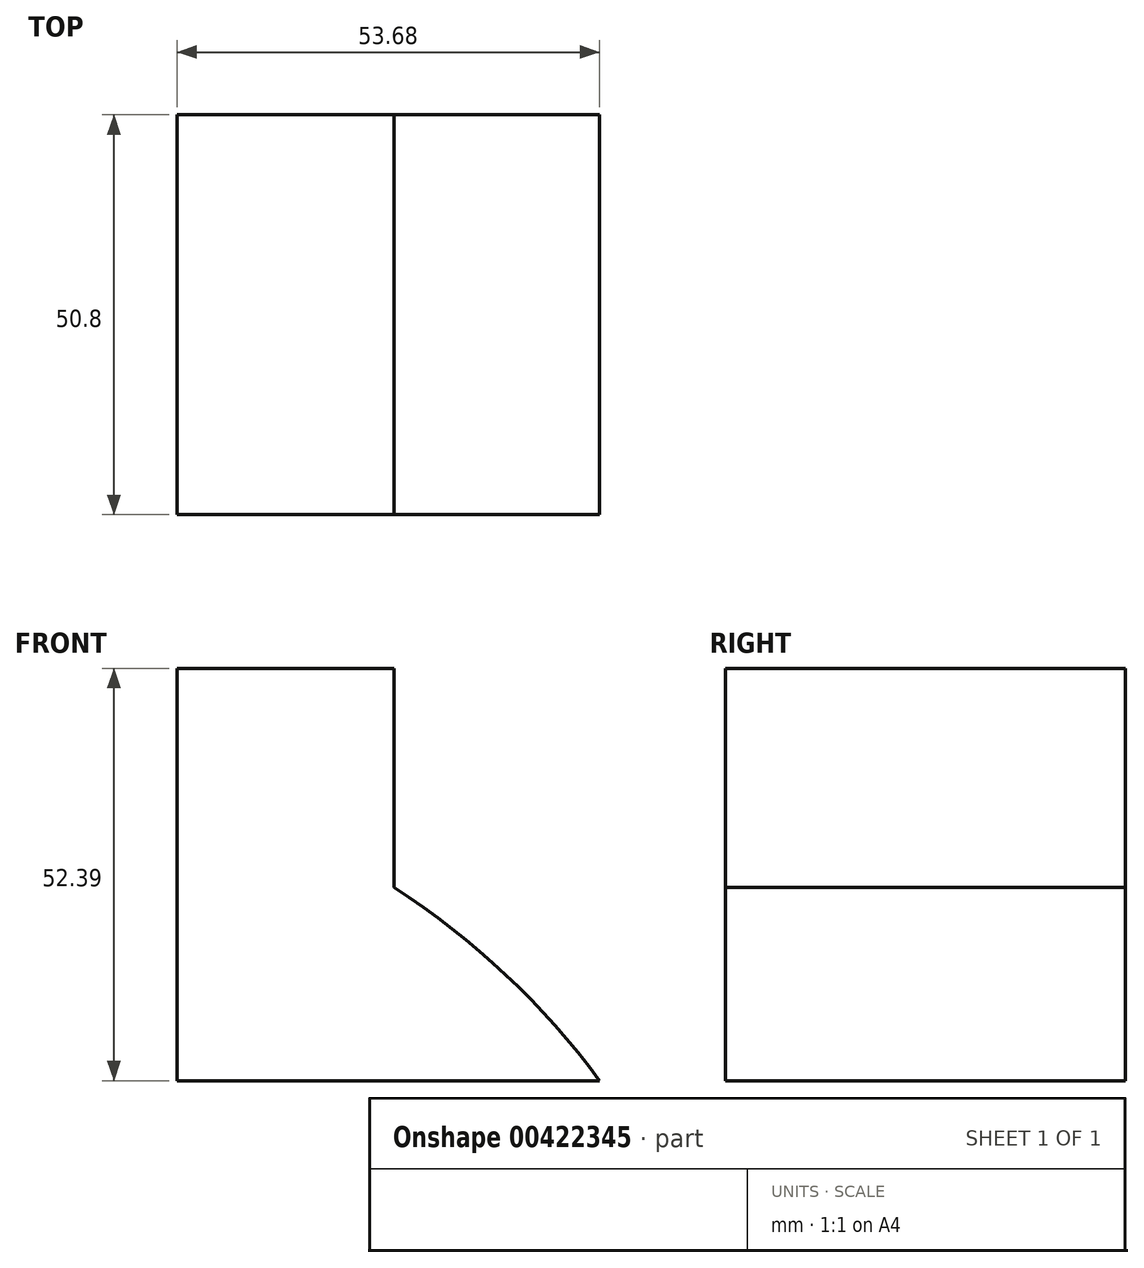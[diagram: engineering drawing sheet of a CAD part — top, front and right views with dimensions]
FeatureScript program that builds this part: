
annotation { "Feature Type Name" : "Feature", "Feature Type Description" : "" }
export const myFeature = defineFeature(function(context is Context, id is Id, definition is map)
    precondition{}
    {
        {
            var Q0;
            Q0=qCreatedBy(makeId("Front.planeOp"),FACE);
            var sketch = newSketch(context, id + "F0", { "sketchPlane" : qUnion([Q0])});
            skLineSegment(sketch, "E0", {"start": v(0, 0) * mm, "end": v(-53.68, 0) * mm});
            skLineSegment(sketch, "E1", {"start": v(-53.68, 0) * mm, "end": v(-53.68, 52.4) * mm});
            skLineSegment(sketch, "E2", {"start": v(-53.68, 52.4) * mm, "end": v(-26.07, 52.4) * mm});
            skLineSegment(sketch, "E3", {"start": v(-26.07, 52.4) * mm, "end": v(-26.07, 24.52) * mm});
            skArc(sketch, "E4", {"start": v(0, 0) * mm, "mid": v(-11.92, 13.45) * mm, "end": v(-26.07, 24.52) * mm});
            skSolve(sketch);
        }
        {
            var Q0;
            Q0 = qSketchRegion(id + "F0", true);
            extrude(context, id + "F1", {"entities" : qUnion([Q0]), "depth" : 50.8 * mm});
        }
    });
